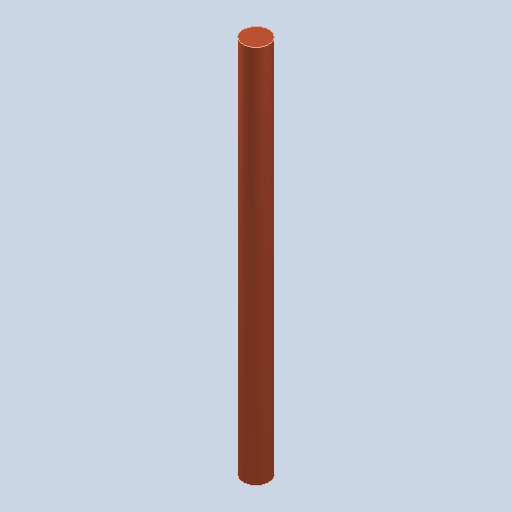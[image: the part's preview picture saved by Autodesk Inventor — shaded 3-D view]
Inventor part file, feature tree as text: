
AUTODESK INVENTOR PART (.ipt)
format: ipt  version: 2024.2 (Build 282272000, 272)  size: 233,472 bytes
history: native  units: mm
features: other x1, extrude x1, sketch x1
ambient origin geometry x8: Origin, YZ Plane, XZ Plane, XY Plane, X Axis, Y Axis, Z Axis, Center Point
bodies: Body1 (feature_tree)
feature tree (3):
  other  "Bryła1"
  extrude  "Wyciągnięcie proste1"  Depth=1.5mm
  sketch  "Szkic1"
